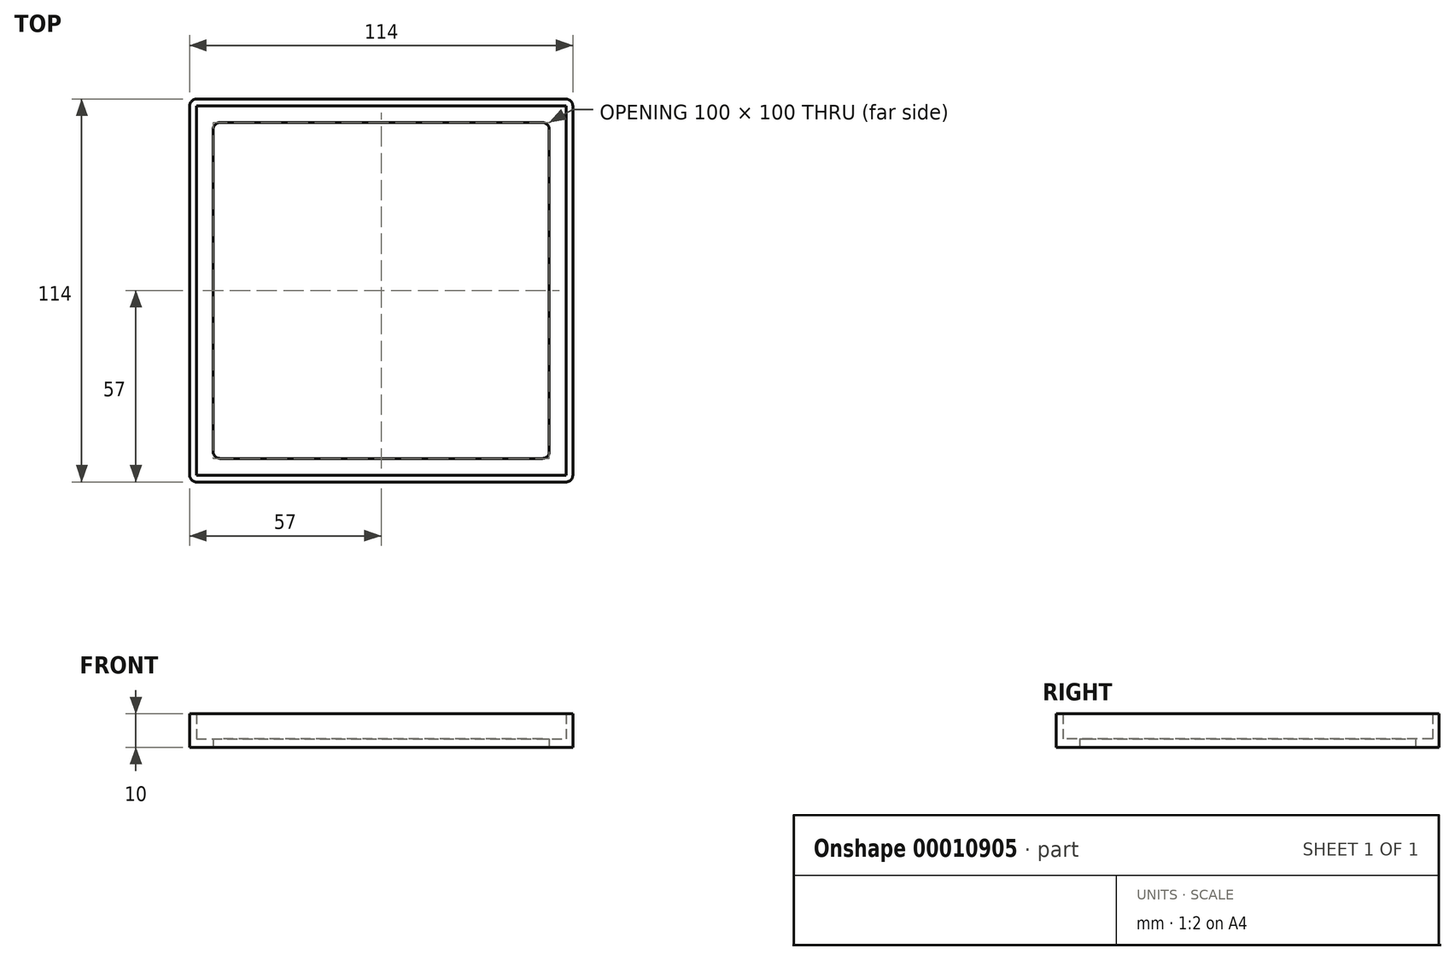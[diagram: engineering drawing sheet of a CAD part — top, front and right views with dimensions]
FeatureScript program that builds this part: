
annotation { "Feature Type Name" : "Feature", "Feature Type Description" : "" }
export const myFeature = defineFeature(function(context is Context, id is Id, definition is map)
    precondition{}
    {
        {
            var Q0;
            Q0=qCreatedBy(makeId("Top.planeOp"),FACE);
            var sketch = newSketch(context, id + "F0", { "sketchPlane" : qUnion([Q0])});
            skLineSegment(sketch, "E0.0", {"start": v(55, 55) * mm, "end": v(-55, 55) * mm});
            skLineSegment(sketch, "E1.0", {"start": v(55, -55) * mm, "end": v(-55, -55) * mm});
            skLineSegment(sketch, "E2.0", {"start": v(55, -55) * mm, "end": v(55, 55) * mm});
            skLineSegment(sketch, "E3.0", {"start": v(-55, -55) * mm, "end": v(-55, 55) * mm});
            skLineSegment(sketch, "E4.0", {"start": v(-50, -50) * mm, "end": v(-50, 50) * mm});
            skLineSegment(sketch, "E5.0", {"start": v(50, 50) * mm, "end": v(-50, 50) * mm});
            skLineSegment(sketch, "E6.0", {"start": v(50, -50) * mm, "end": v(50, 50) * mm});
            skLineSegment(sketch, "E7.0", {"start": v(50, -50) * mm, "end": v(-50, -50) * mm});
            skLineSegment(sketch, "E8.0", {"start": v(57, -57) * mm, "end": v(-57, -57) * mm});
            skLineSegment(sketch, "E9.0", {"start": v(-57, -57) * mm, "end": v(-57, 57) * mm});
            skLineSegment(sketch, "E10.0", {"start": v(57, 57) * mm, "end": v(-57, 57) * mm});
            skLineSegment(sketch, "E11.0", {"start": v(57, -57) * mm, "end": v(57, 57) * mm});
            skSolve(sketch);
        }
        {
            var Q0;
            Q0 = qSketchRegion(id + "F0", true);
            var Q1;
            Q1=makeQuery(id+"F0.imprint","IMPRINT",FACE,{"disambiguationData":[TD([[makeQuery(id+"F0.imprint","IMPRINT",EDGE,{"derivedFrom":sQuery(id+"F0.wireOp",EDGE,"E0.0")}),1.0]])]});
            extrude(context, id + "F1", {"entities" : qUnion([Q0, Q1]), "depth" : 2.5 * mm});
        }
        {
            var Q0;
            Q0=makeQuery(id+"F0.imprint","IMPRINT",FACE,{"disambiguationData":[TD([[makeQuery(id+"F0.imprint","IMPRINT",EDGE,{"derivedFrom":sQuery(id+"F0.wireOp",EDGE,"E0.0")}),-1.0]])]});
            extrude(context, id + "F2", {"entities" : qUnion([Q0]), "operationType" : NewBodyOperationType.ADD, "depth" : 10 * mm});
        }
        {
            var Q0;
            {var subQ0=sQuery(id+"F0.wireOp",EDGE,"E8.0");var subQ1=sQuery(id+"F0.wireOp",EDGE,"E9.0");Q0=makeQuery(id+"F2.boolean.opBoolean","MERGE",EDGE,{"derivedFrom":[makeQuery(id+"F1.opExtrude","SWEPT_EDGE",EDGE,{"disambiguationData":[OSD([subQ0,subQ1])]}),makeQuery(id+"F2.opExtrude","SWEPT_EDGE",EDGE,{"disambiguationData":[OSD([subQ0,subQ1])]})]});}
            var Q1;
            {var subQ0=sQuery(id+"F0.wireOp",EDGE,"E8.0");var subQ1=sQuery(id+"F0.wireOp",EDGE,"E11.0");Q1=makeQuery(id+"F2.boolean.opBoolean","MERGE",EDGE,{"derivedFrom":[makeQuery(id+"F1.opExtrude","SWEPT_EDGE",EDGE,{"disambiguationData":[OSD([subQ0,subQ1])]}),makeQuery(id+"F2.opExtrude","SWEPT_EDGE",EDGE,{"disambiguationData":[OSD([subQ0,subQ1])]})]});}
            var Q2;
            {var subQ0=sQuery(id+"F0.wireOp",EDGE,"E10.0");var subQ1=sQuery(id+"F0.wireOp",EDGE,"E11.0");Q2=makeQuery(id+"F2.boolean.opBoolean","MERGE",EDGE,{"derivedFrom":[makeQuery(id+"F1.opExtrude","SWEPT_EDGE",EDGE,{"disambiguationData":[OSD([subQ0,subQ1])]}),makeQuery(id+"F2.opExtrude","SWEPT_EDGE",EDGE,{"disambiguationData":[OSD([subQ0,subQ1])]})]});}
            var Q3;
            {var subQ0=sQuery(id+"F0.wireOp",EDGE,"E9.0");var subQ1=sQuery(id+"F0.wireOp",EDGE,"E10.0");Q3=makeQuery(id+"F2.boolean.opBoolean","MERGE",EDGE,{"derivedFrom":[makeQuery(id+"F1.opExtrude","SWEPT_EDGE",EDGE,{"disambiguationData":[OSD([subQ0,subQ1])]}),makeQuery(id+"F2.opExtrude","SWEPT_EDGE",EDGE,{"disambiguationData":[OSD([subQ0,subQ1])]})]});}
            var Q4;
            Q4=makeQuery(id+"F1.opExtrude","SWEPT_EDGE",EDGE,{"disambiguationData":[OSD([sQuery(id+"F0.wireOp",EDGE,"E4.0"),sQuery(id+"F0.wireOp",EDGE,"E7.0")])]});
            var Q5;
            Q5=makeQuery(id+"F1.opExtrude","SWEPT_EDGE",EDGE,{"disambiguationData":[OSD([sQuery(id+"F0.wireOp",EDGE,"E4.0"),sQuery(id+"F0.wireOp",EDGE,"E5.0")])]});
            var Q6;
            Q6=makeQuery(id+"F1.opExtrude","SWEPT_EDGE",EDGE,{"disambiguationData":[OSD([sQuery(id+"F0.wireOp",EDGE,"E6.0"),sQuery(id+"F0.wireOp",EDGE,"E7.0")])]});
            var Q7;
            Q7=makeQuery(id+"F1.opExtrude","SWEPT_EDGE",EDGE,{"disambiguationData":[OSD([sQuery(id+"F0.wireOp",EDGE,"E5.0"),sQuery(id+"F0.wireOp",EDGE,"E6.0")])]});
            fillet(context, id + "F3", {"entities" : qUnion([Q0, Q1, Q2, Q3, Q4, Q5, Q6, Q7]), "radius" : 2 * mm, "tangentPropagation" : true, "allowEdgeOverflow" : false});
        }
    });
